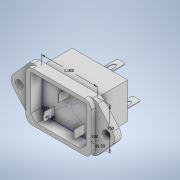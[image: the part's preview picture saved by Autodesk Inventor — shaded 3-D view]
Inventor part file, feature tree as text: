
AUTODESK INVENTOR PART (.ipt)
format: ipt  version: 2022.1 (Build 261234000, 234)  size: 351,232 bytes
history: native  units: in
note: dims shown in document units (in); Inventor stores cm internally (conversion verified against a paired STEP export)
features: extrude x9, sketch x7, fillet x1, chamfer x1
ambient origin geometry x8: Origin, YZ Plane, XZ Plane, XY Plane, X Axis, Y Axis, Z Axis, Center Point
bodies: Solid1 (feature_tree)
feature tree (18):
  extrude  "Extrusion1"  Depth=0.89in
  extrude  "Extrusion2"  Depth=1.0in
  extrude  "Extrusion3"  TaperAngle=45.0deg  [1 undecoded]
  extrude  "Extrusion4"  TaperAngle=45.0deg  [1 undecoded]
  extrude  "Extrusion5"  Depth=0.0in TaperAngle=0.0deg
  extrude  "Extrusion6"  Depth=0.3in
  extrude  "Extrusion7"  Depth=0.125in
  extrude  "Extrusion8"  Depth=0.125in
  extrude  "Extrusion9"  Depth=0.118in TaperAngle=0.0deg
  fillet  "Fillet1"  Radius=0.197in
  chamfer  "Chamfer1"  Distance=0.551in
  sketch  "Sketch1"  dims[d0=1.185in d1=0.89in]
  sketch  "Sketch2"  dims[d2=0.551in d3=0.0in d4=1.0in]
  sketch  "Sketch4"  dims[d5=0.75in d9=45.0deg]
  sketch  "Sketch5"  dims[d10=0.1in d11=45.0deg]
  sketch  "Sketch6"  dims[d12=0.1in d13=0.0in d14=0.0in]
  sketch  "Sketch7"  dims[d17=0.138in d19=0.3in]
  sketch  "Sketch8"  dims[d20=0.3in d21=0.3067in d24=0.7875in d25=0.118in d26=0.0in d27=0.197in d28=0.0in d29=0.551in d30=0.0in d32=0.075in d36=0.075in d37=0.075in d38=0.075in d39=0.075in d40=0.1in d41=0.06in d42=1.0063in d43=0.06in d44=0.075in d45=0.06in d46=0.075in d47=0.06in d48=0.075in d49=0.1in d50=0.075in d51=0.06in d52=0.005in d53=0.0in d54=0.01in d55=0.01in d56=0.01in d57=0.384in d58=0.0in d59=0.097in d60=0.039in d61=0.097in d62=0.097in d63=0.039in d64=0.039in d65=0.075in d66=0.075in d67=0.075in d68=0.1945in d69=0.1945in d70=0.0in d71=0.0in d75=0.01in d79=90.0deg d80=0.15in d81=0.01in d82=0.15in d83=0.01in d84=0.005in d89=0.01in d90=0.15in d91=0.01in d92=0.005in d93=0.07in d94=0.197in d95=0.0in d96=0.125in d97=0.02in d98=0.125in d99=45.0deg]
note: 2 required parameter values undecoded (feature->parameter linkage not recoverable at this tier; creation-order binding heuristic only, values carry confidence <= 0.55)
